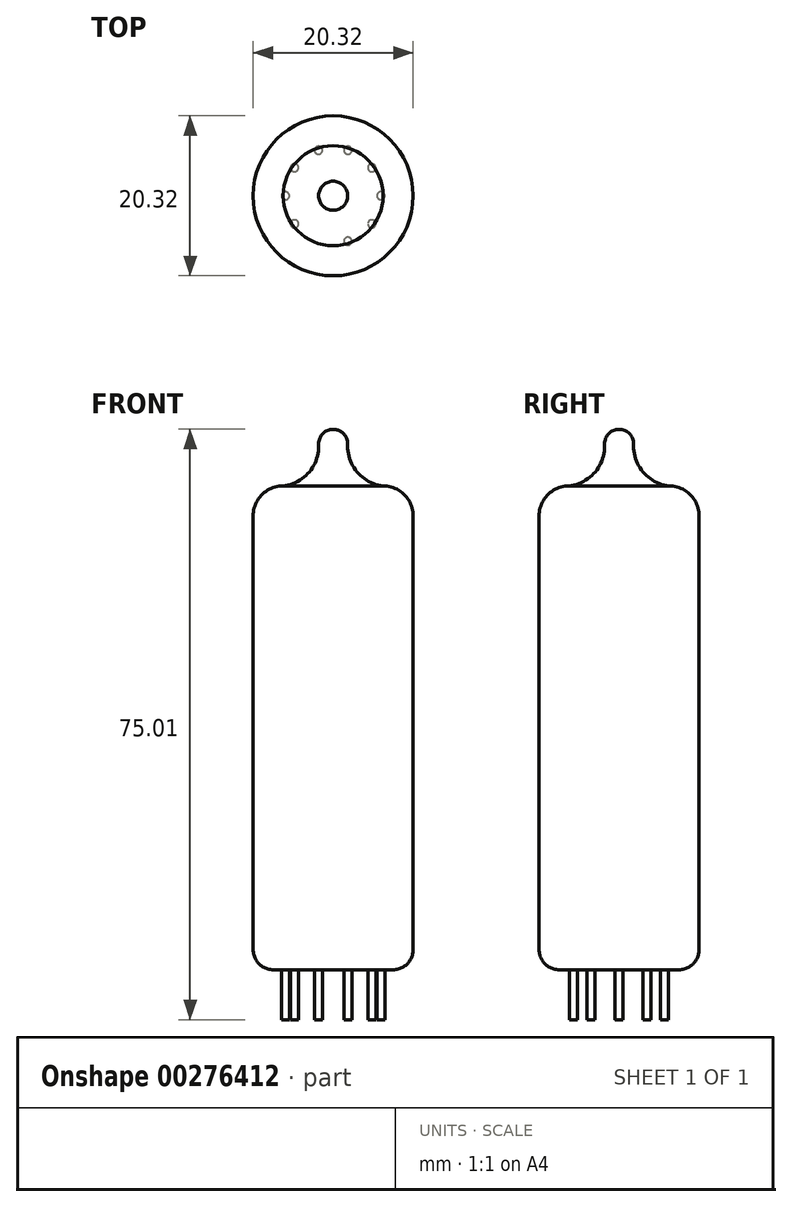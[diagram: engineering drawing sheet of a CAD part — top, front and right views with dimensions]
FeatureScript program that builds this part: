
annotation { "Feature Type Name" : "Feature", "Feature Type Description" : "" }
export const myFeature = defineFeature(function(context is Context, id is Id, definition is map)
    precondition{}
    {
        {
            var Q0;
            Q0=qCreatedBy(makeId("Front.planeOp"),FACE);
            var sketch = newSketch(context, id + "F0", { "sketchPlane" : qUnion([Q0])});
            skLineSegment(sketch, "E0", {"start": v(0, 73.58) * mm, "end": v(0, -16.17) * mm, "construction": true});
            skLineSegment(sketch, "E1", {"start": v(0, 0) * mm, "end": v(7.62, 0) * mm});
            skLineSegment(sketch, "E2", {"start": v(10.16, 2.54) * mm, "end": v(10.16, 57.66) * mm});
            skLineSegment(sketch, "E3", {"start": v(1.84, 66.52) * mm, "end": v(1.84, 66.81) * mm});
            skArc(sketch, "E4", {"start": v(1.84, 66.81) * mm, "mid": v(1.3, 68.12) * mm, "end": v(0, 68.66) * mm});
            skArc(sketch, "E5.filletArc", {"start": v(1.84, 66.52) * mm, "mid": v(3.13, 63.13) * mm, "end": v(6.35, 61.47) * mm});
            skArc(sketch, "E6.filletArc", {"start": v(10.16, 57.66) * mm, "mid": v(9.04, 60.35) * mm, "end": v(6.35, 61.47) * mm});
            skArc(sketch, "E7.filletArc", {"start": v(7.62, 0) * mm, "mid": v(9.42, 0.74) * mm, "end": v(10.16, 2.54) * mm});
            skLineSegment(sketch, "E8", {"start": v(0, 68.66) * mm, "end": v(0, 0) * mm});
            skSolve(sketch);
        }
        {
            var Q0;
            Q0 = qSketchRegion(id + "F0", true);
            var Q1;
            Q1=sQuery(id+"F0.wireOp",EDGE,"E0");
            revolve(context, id + "F1", {"entities" : qUnion([Q0]), "axis" : qUnion([Q1]), "revolveType" : RevolveType.FULL});
        }
        {
            var Q0;
            Q0=makeQuery(id+"F1.opRevolve","SWEPT_FACE",FACE,{"disambiguationData":[OSD([sQuery(id+"F0.wireOp",EDGE,"E1")])]});
            var sketch = newSketch(context, id + "F2", { "sketchPlane" : qUnion([Q0])});
            skCircle(sketch, "E9", {"center": v(0, 0) * mm, "radius": 6.58 * mm, "construction": true});
            skCircle(sketch, "E10", {"center": v(-6.07, 0) * mm, "radius": 0.5 * mm});
            skCircle(sketch, "E11", {"center": v(6.07, 0) * mm, "radius": 0.5 * mm});
            skCircle(sketch, "E12", {"center": v(-4.91, -3.57) * mm, "radius": 0.5 * mm});
            skCircle(sketch, "E13", {"center": v(-1.88, -5.77) * mm, "radius": 0.5 * mm});
            skCircle(sketch, "E14", {"center": v(1.88, -5.77) * mm, "radius": 0.5 * mm});
            skCircle(sketch, "E15", {"center": v(4.91, -3.57) * mm, "radius": 0.5 * mm});
            skCircle(sketch, "E16", {"center": v(4.91, 3.57) * mm, "radius": 0.5 * mm});
            skCircle(sketch, "E17", {"center": v(1.88, 5.77) * mm, "radius": 0.5 * mm});
            skCircle(sketch, "E18", {"center": v(-4.91, 3.57) * mm, "radius": 0.5 * mm});
            skLineSegment(sketch, "E19", {"start": v(-4.91, -3.57) * mm, "end": v(4.91, 3.57) * mm, "construction": true});
            skLineSegment(sketch, "E20", {"start": v(-4.91, 3.57) * mm, "end": v(4.91, -3.57) * mm, "construction": true});
            skLineSegment(sketch, "E21", {"start": v(-1.88, -5.77) * mm, "end": v(1.88, 5.77) * mm, "construction": true});
            skCircle(sketch, "E22", {"center": v(-1.88, 5.77) * mm, "radius": 0.5 * mm, "construction": true});
            skLineSegment(sketch, "E23", {"start": v(1.88, -5.77) * mm, "end": v(-1.88, 5.77) * mm, "construction": true});
            skSolve(sketch);
        }
        {
            var Q0;
            Q0 = qSketchRegion(id + "F2", true);
            extrude(context, id + "F3", {"entities" : qUnion([Q0]), "operationType" : NewBodyOperationType.ADD, "depth" : 6.35 * mm});
        }
    });
